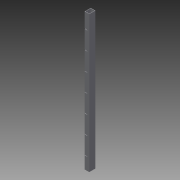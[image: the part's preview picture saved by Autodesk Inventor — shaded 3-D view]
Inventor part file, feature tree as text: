
AUTODESK INVENTOR PART (.ipt)
format: ipt  version: 2013 (Build 170138000, 138)  size: 129,024 bytes
history: native  units: in
note: dims shown in document units (in); Inventor stores cm internally (conversion verified against a paired STEP export)
features: other x3, sketch x1
ambient origin geometry x8: Origin, YZ Plane, XZ Plane, XY Plane, X Axis, Y Axis, Z Axis, Center Point
bodies: Solid1 (feature_tree)
feature tree (4):
  other  "tableFrameSide.ipt"
  other  "Solid1::tableFrameSide.ipt"
  other  "TaggingFeature1"
  sketch  "Sketch2"  dims[d0=0.3937in d20=2.7559in d22=6.0in d27=1.0in d28=0.0in d29=0.1875in d30=4.0in d31=0.75in d4=0.0in d2=0.125in d1=2.0in]
